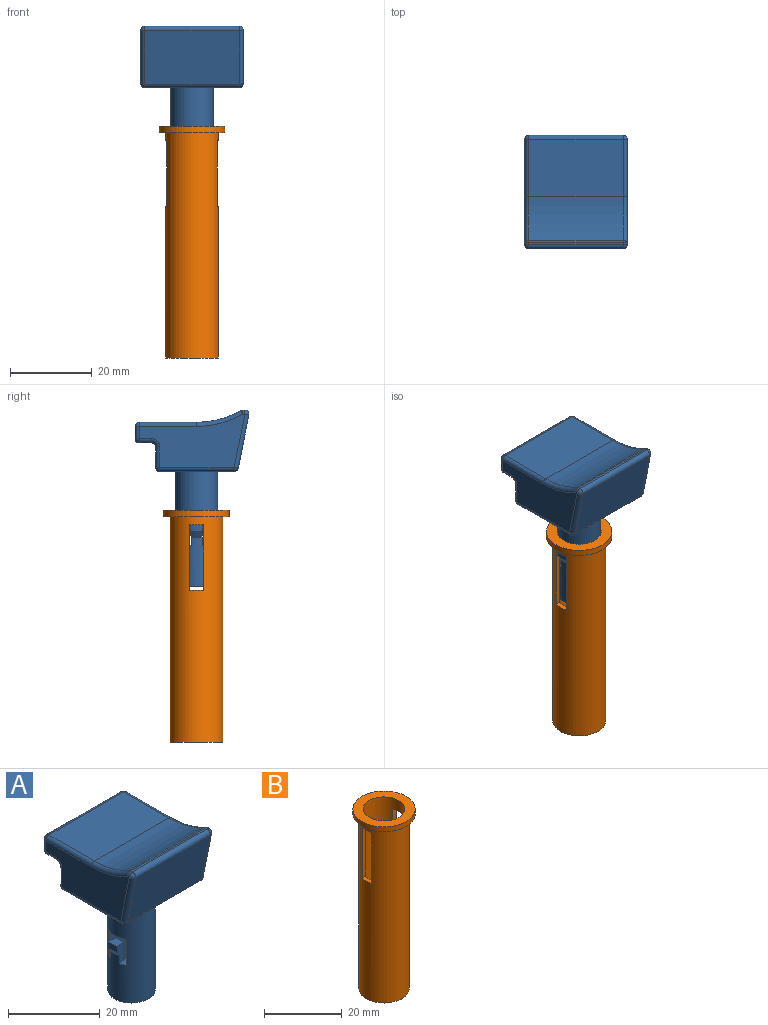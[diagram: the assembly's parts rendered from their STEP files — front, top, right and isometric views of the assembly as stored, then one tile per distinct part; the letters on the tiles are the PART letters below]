
ASSEMBLY  parts=2 mates=1
PART A: 71 faces, bbox 25x27.8x43 mm
  f0: cylinder r=3.2mm len=28mm, axis (0,0,1), area 470.3mm2, adj f2,f20,f51,f52,f53,f54,f55,f56
  f1: cylinder r=5.2mm len=28mm, axis (0,0,1), area 844.6mm2, adj f2,f11,f51,f52,f53,f54,f55,f56
  f2: plane 10.4x10.4mm, normal (0,0,-1), area 52.8mm2, adj f0,f1
  f3: plane 25.78x13mm, normal (-1,0,0), area 219.2mm2, adj f21,f24,f25,f28,f29,f30,f31,f33
  f4: plane 25.78x13mm, normal (1,0,0), area 219.2mm2, adj f36,f39,f40,f43,f44,f45,f46,f48
  f5: plane 23x3mm, normal (0,1,0), area 69mm2, adj f6,f19,f34,f49
  f6: cylinder r=1mm len=23mm, axis (-1,0,0), area 36.1mm2, adj f5,f7,f35,f50
  f7: plane 23x3mm, normal (0,0,-1), area 69mm2, adj f6,f8,f33,f48
  f8: cylinder r=1mm len=23mm, axis (-1,0,0), area 36.1mm2, adj f7,f9,f31,f46
  f9: plane 23x5mm, normal (0,1,0), area 115mm2, adj f8,f10,f29,f44
  f10: cylinder r=1mm len=23mm, axis (-1,0,0), area 36.1mm2, adj f9,f11,f27,f42
  f11: plane 23x18.18mm, normal (0,0,-1), area 333.2mm2, adj f1,f10,f12,f25,f40
  f12: cylinder r=1mm len=23mm, axis (-1,0,0), area 31.6mm2, adj f11,f13,f23,f38
  f13: plane 23x13mm, normal (0,-0.98,-0.2), area 304.9mm2, adj f12,f14,f21,f36
  f14: cylinder r=1mm len=23mm, axis (-1,0,0), area 40.7mm2, adj f13,f15,f22,f37
  f15: plane 23x0.51mm, normal (0,0,1), area 11.7mm2, adj f14,f16,f24,f39
  f16: cylinder r=1mm len=23mm, axis (-1,0,0), area 12mm2, adj f15,f17,f26,f41
  f17: cylinder r=21.67mm len=23mm, axis (-1,0,0), area 259.3mm2, adj f16,f18,f28,f43
  f18: plane 23x14mm, normal (0,0,1), area 322mm2, adj f17,f19,f30,f45
  f19: cylinder r=1mm len=23mm, axis (-1,0,0), area 36.1mm2, adj f5,f18,f32,f47
  f20: plane 6.4x6.4mm, normal (0,0,-1), area 32.2mm2, adj f0
  f21: cylinder r=1mm len=13.2mm, axis (0,0.2,-0.98), area 20.8mm2, adj f3,f13,f22,f23
  f22: sphere r=1mm, area 1.8mm2, adj f14,f21,f24
  f23: sphere r=1mm, area 1.4mm2, adj f12,f21,f25
  f24: cylinder r=1mm len=1mm, axis (0,-1,0), area 0.8mm2, adj f3,f15,f22,f26
  f25: cylinder r=1mm len=18.18mm, axis (0,1,0), area 28.6mm2, adj f3,f11,f23,f27
  f26: sphere r=1mm, area 0.5mm2, adj f16,f24,f28
  f27: sphere r=1mm, area 1.6mm2, adj f10,f25,f29
  f28: torus R=22.67mm, axis (1,0,0), area 18mm2, adj f3,f17,f26,f30
  f29: cylinder r=1mm len=5mm, axis (0,0,1), area 7.9mm2, adj f3,f9,f27,f31
  f30: cylinder r=1mm len=14mm, axis (0,-1,0), area 22mm2, adj f3,f18,f28,f32
  f31: torus R=2mm, axis (1,0,0), area 3.4mm2, adj f3,f8,f29,f33
  f32: sphere r=1mm, area 1.6mm2, adj f19,f30,f34
  f33: cylinder r=1mm len=3mm, axis (0,1,0), area 4.7mm2, adj f3,f7,f31,f35
  f34: cylinder r=1mm len=3mm, axis (0,0,1), area 4.7mm2, adj f3,f5,f32,f35
  f35: sphere r=1mm, area 1.6mm2, adj f6,f33,f34
  f36: cylinder r=1mm len=13.2mm, axis (0,-0.2,0.98), area 20.8mm2, adj f4,f13,f37,f38
  f37: sphere r=1mm, area 1.8mm2, adj f14,f36,f39
  f38: sphere r=1mm, area 1.4mm2, adj f12,f36,f40
  f39: cylinder r=1mm len=1mm, axis (0,1,0), area 0.8mm2, adj f4,f15,f37,f41
  f40: cylinder r=1mm len=18.18mm, axis (0,-1,0), area 28.6mm2, adj f4,f11,f38,f42
  f41: sphere r=1mm, area 0.5mm2, adj f16,f39,f43
  f42: sphere r=1mm, area 1.6mm2, adj f10,f40,f44
  f43: torus R=22.67mm, axis (1,0,0), area 18mm2, adj f4,f17,f41,f45
  f44: cylinder r=1mm len=5mm, axis (0,0,-1), area 7.9mm2, adj f4,f9,f42,f46
  f45: cylinder r=1mm len=14mm, axis (0,1,0), area 22mm2, adj f4,f18,f43,f47
  f46: torus R=2mm, axis (1,0,0), area 3.4mm2, adj f4,f8,f44,f48
  f47: sphere r=1mm, area 1.6mm2, adj f19,f45,f49
  f48: cylinder r=1mm len=3mm, axis (0,-1,0), area 4.7mm2, adj f4,f7,f46,f50
  f49: cylinder r=1mm len=3mm, axis (0,0,-1), area 4.7mm2, adj f4,f5,f47,f50
  f50: sphere r=1mm, area 1.6mm2, adj f6,f48,f49
  f51: plane 7x2.78mm, normal (0,1,0), area 19.4mm2, adj f0,f1,f52,f54
  f52: plane 5.5x3.56mm, normal (0,0,-1), area 12.1mm2, adj f0,f1,f51,f53
  f53: plane 7x2.78mm, normal (0,-1,0), area 19.4mm2, adj f0,f1,f52,f54
  f54: plane 5.5x3.39mm, normal (0,0,1), area 8.6mm2, adj f0,f1,f51,f53,f59,f63,f64
  f55: plane 5.5x3.39mm, normal (0,0,1), area 8.6mm2, adj f0,f1,f56,f58,f65,f69,f70
  f56: plane 7x2.78mm, normal (0,-1,0), area 19.4mm2, adj f0,f1,f55,f57
  f57: plane 5.5x3.56mm, normal (0,0,-1), area 12.1mm2, adj f0,f1,f56,f58
  f58: plane 7x2.78mm, normal (0,1,0), area 19.4mm2, adj f0,f1,f55,f57
  f59: cylinder r=3.7mm len=5mm, axis (0,0,1), area 9.7mm2, adj f54,f62,f63,f64
  f60: cone r=5.2mm half-angle=30deg, axis (0,0,1), area 4.7mm2, adj f1,f61,f63,f64
  f61: cylinder r=6mm len=3.11mm, axis (0,0,1), area 5.1mm2, adj f60,f62,f63,f64
  f62: plane 3.11x2.43mm, normal (0,0,1), area 5.8mm2, adj f59,f61,f63,f64
  f63: plane 5x2.22mm, normal (-0.26,-0.97,0), area 9.3mm2, adj f1,f54,f59,f60,f61,f62
  f64: plane 5x2.22mm, normal (-0.26,0.97,0), area 9.3mm2, adj f1,f54,f59,f60,f61,f62
  f65: cylinder r=3.7mm len=5mm, axis (0,0,1), area 9.7mm2, adj f55,f68,f69,f70
  f66: cone r=5.2mm half-angle=30deg, axis (0,0,1), area 4.7mm2, adj f1,f67,f69,f70
  f67: cylinder r=6mm len=3.11mm, axis (0,0,1), area 5.1mm2, adj f66,f68,f69,f70
  f68: plane 3.11x2.43mm, normal (0,0,1), area 5.8mm2, adj f65,f67,f69,f70
  f69: plane 5x2.22mm, normal (0.26,-0.97,0), area 9.3mm2, adj f1,f55,f65,f66,f67,f68
  f70: plane 5x2.22mm, normal (0.26,0.97,0), area 9.3mm2, adj f1,f55,f65,f66,f67,f68
PART B: 15 faces, bbox 16x16x56.5 mm
  f0: cylinder r=5.35mm len=55.4mm, axis (0,0,-1), area 1744.8mm2, adj f3,f6,f7,f8,f9,f10,f11,f12
  f1: cylinder r=6.45mm len=55mm, axis (0,0,1), area 2112.2mm2, adj f4,f5,f7,f8,f9,f10,f11,f12
  f2: cylinder r=8mm len=16mm, axis (0,0,-1), area 75.4mm2, adj f3,f4
  f3: plane 16x16mm, normal (0,0,1), area 111.1mm2, adj f0,f2
  f4: plane 16x16mm, normal (0,0,-1), area 70.4mm2, adj f1,f2
  f5: plane 12.9x12.9mm, normal (0,0,-1), area 130.7mm2, adj f1
  f6: plane 10.7x10.7mm, normal (0,0,1), area 89.9mm2, adj f0
  f7: plane 16x1.16mm, normal (0,1,0), area 18.5mm2, adj f0,f1,f8,f10
  f8: plane 3.6x1.41mm, normal (0,0,-1), area 4mm2, adj f0,f1,f7,f9
  f9: plane 16x1.16mm, normal (0,-1,0), area 18.5mm2, adj f0,f1,f8,f10
  f10: plane 3.6x1.41mm, normal (0,0,1), area 4mm2, adj f0,f1,f7,f9
  f11: plane 3.6x1.41mm, normal (0,0,1), area 4mm2, adj f0,f1,f12,f14
  f12: plane 16x1.16mm, normal (0,-1,0), area 18.5mm2, adj f0,f1,f11,f13
  f13: plane 3.6x1.41mm, normal (0,0,-1), area 4mm2, adj f0,f1,f12,f14
  f14: plane 16x1.16mm, normal (0,1,0), area 18.5mm2, adj f0,f1,f11,f13
PLACE A t=(0,0,11)mm
PLACE B at identity fixed
MATE slider B.f0 <-> A.f1  axis (0,0,1) through (0,0,1.5)mm
